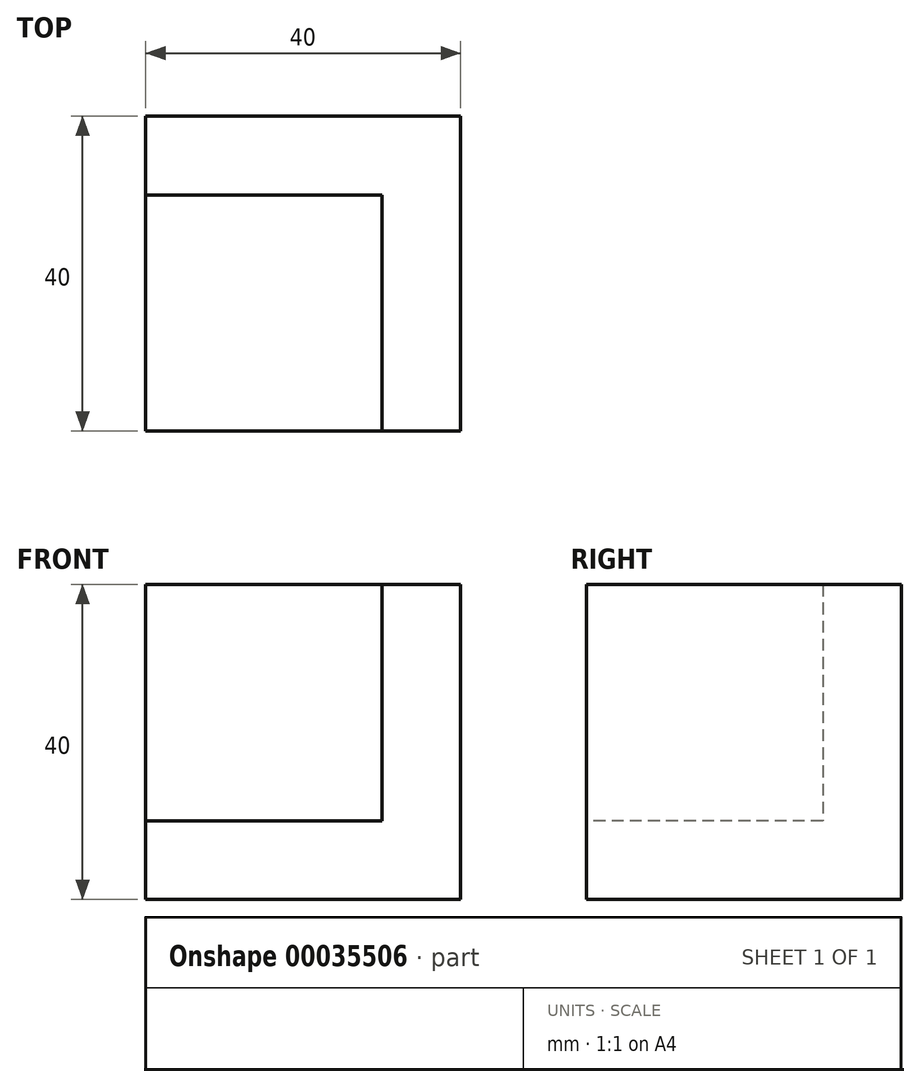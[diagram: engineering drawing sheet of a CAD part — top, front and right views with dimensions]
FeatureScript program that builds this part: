
annotation { "Feature Type Name" : "Feature", "Feature Type Description" : "" }
export const myFeature = defineFeature(function(context is Context, id is Id, definition is map)
    precondition{}
    {
        {
            var Q0;
            Q0=qCreatedBy(makeId("Top.planeOp"),FACE);
            var sketch = newSketch(context, id + "F0", { "sketchPlane" : qUnion([Q0])});
            skLineSegment(sketch, "E0.bottom", {"start": v(-21.8, 24.16) * mm, "end": v(18.2, 24.16) * mm});
            skLineSegment(sketch, "E0.top", {"start": v(-21.8, -15.84) * mm, "end": v(18.2, -15.84) * mm});
            skLineSegment(sketch, "E0.left", {"start": v(-21.8, 24.16) * mm, "end": v(-21.8, -15.84) * mm});
            skLineSegment(sketch, "E0.right", {"start": v(18.2, 24.16) * mm, "end": v(18.2, -15.84) * mm});
            skSolve(sketch);
        }
        {
            var Q0;
            Q0=makeQuery(id+"F0.imprint","IMPRINT",FACE,{"disambiguationData":[TD([[makeQuery(id+"F0.imprint","IMPRINT",EDGE,{"derivedFrom":sQuery(id+"F0.wireOp",EDGE,"E0.bottom")}),-1.0]])]});
            extrude(context, id + "F1", {"entities" : qUnion([Q0]), "depth" : 40 * mm});
        }
        {
            var Q0;
            Q0=makeQuery(id+"F1.opExtrude","SWEPT_FACE",FACE,{"disambiguationData":[OSD([sQuery(id+"F0.wireOp",EDGE,"E0.top")])]});
            var sketch = newSketch(context, id + "F2", { "sketchPlane" : qUnion([Q0])});
            skLineSegment(sketch, "E1.bottom", {"start": v(-21.8, 40) * mm, "end": v(8.2, 40) * mm});
            skLineSegment(sketch, "E1.top", {"start": v(-21.8, 10) * mm, "end": v(8.2, 10) * mm});
            skLineSegment(sketch, "E1.left", {"start": v(-21.8, 40) * mm, "end": v(-21.8, 10) * mm});
            skLineSegment(sketch, "E1.right", {"start": v(8.2, 40) * mm, "end": v(8.2, 10) * mm});
            skSolve(sketch);
        }
        {
            var Q0;
            Q0=makeQuery(id+"F2.imprint","IMPRINT",FACE,{"disambiguationData":[TD([[makeQuery(id+"F2.imprint","IMPRINT",EDGE,{"derivedFrom":sQuery(id+"F2.wireOp",EDGE,"E1.bottom")}),-1.0]])]});
            extrude(context, id + "F3", {"entities" : qUnion([Q0]), "operationType" : NewBodyOperationType.REMOVE, "oppositeDirection" : true, "depth" : 30 * mm});
        }
    });
